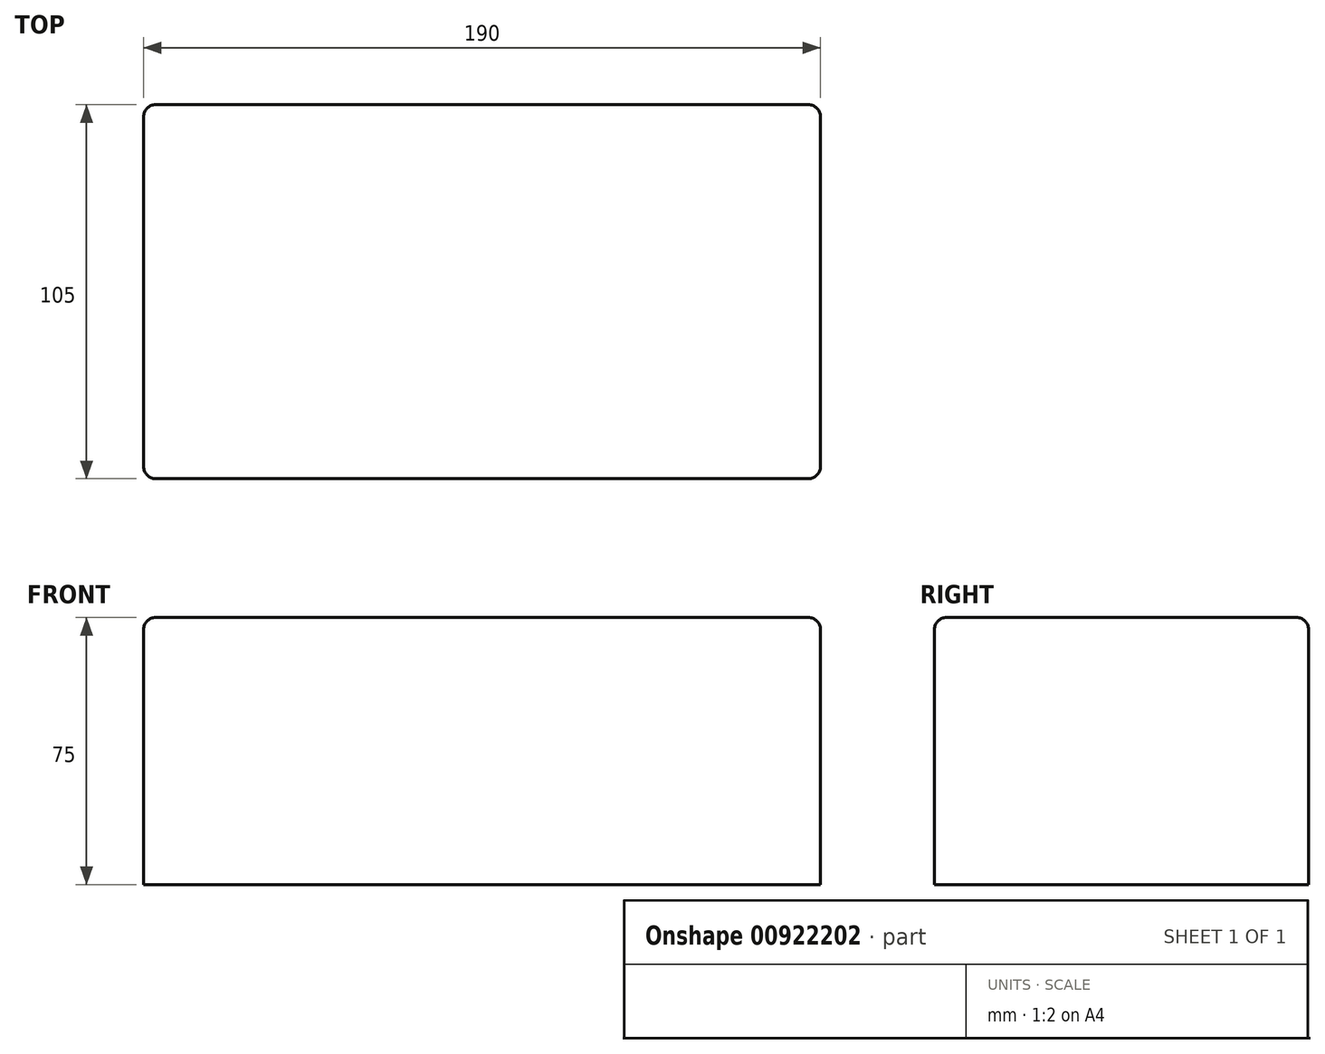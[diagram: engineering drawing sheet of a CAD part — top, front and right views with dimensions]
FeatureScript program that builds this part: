
annotation { "Feature Type Name" : "Feature", "Feature Type Description" : "" }
export const myFeature = defineFeature(function(context is Context, id is Id, definition is map)
    precondition{}
    {
        {
            var Q0;
            Q0=qCreatedBy(makeId("Top.planeOp"),FACE);
            var sketch = newSketch(context, id + "F0", { "sketchPlane" : qUnion([Q0])});
            skLineSegment(sketch, "E0.bottom", {"start": v(-95, 52.5) * mm, "end": v(95, 52.5) * mm});
            skLineSegment(sketch, "E0.top", {"start": v(-95, -52.5) * mm, "end": v(95, -52.5) * mm});
            skLineSegment(sketch, "E0.left", {"start": v(-95, 52.5) * mm, "end": v(-95, -52.5) * mm});
            skLineSegment(sketch, "E0.right", {"start": v(95, 52.5) * mm, "end": v(95, -52.5) * mm});
            skPoint(sketch, "E0.middle", {"position": v(0, 0) * mm});
            skSolve(sketch);
        }
        {
            var Q0;
            Q0 = qSketchRegion(id + "F0", true);
            extrude(context, id + "F1", {"entities" : qUnion([Q0]), "depth" : 75 * mm, "offsetDistance" : 25 * mm});
        }
        {
            var Q0;
            Q0=makeQuery(id+"F1.opExtrude","CAP_EDGE",EDGE,{"disambiguationData":[OSD([sQuery(id+"F0.wireOp",EDGE,"E0.top")])],"isStart":false});
            var Q1;
            Q1=makeQuery(id+"F1.opExtrude","CAP_EDGE",EDGE,{"disambiguationData":[OSD([sQuery(id+"F0.wireOp",EDGE,"E0.left")])],"isStart":false});
            var Q2;
            Q2=makeQuery(id+"F1.opExtrude","CAP_EDGE",EDGE,{"disambiguationData":[OSD([sQuery(id+"F0.wireOp",EDGE,"E0.bottom")])],"isStart":false});
            var Q3;
            Q3=makeQuery(id+"F1.opExtrude","CAP_EDGE",EDGE,{"disambiguationData":[OSD([sQuery(id+"F0.wireOp",EDGE,"E0.right")])],"isStart":false});
            var Q4;
            Q4=makeQuery(id+"F1.opExtrude","SWEPT_EDGE",EDGE,{"disambiguationData":[OSD([sQuery(id+"F0.wireOp",EDGE,"E0.top"),sQuery(id+"F0.wireOp",EDGE,"E0.right")])]});
            var Q5;
            Q5=makeQuery(id+"F1.opExtrude","SWEPT_EDGE",EDGE,{"disambiguationData":[OSD([sQuery(id+"F0.wireOp",EDGE,"E0.top"),sQuery(id+"F0.wireOp",EDGE,"E0.left")])]});
            var Q6;
            Q6=makeQuery(id+"F1.opExtrude","SWEPT_EDGE",EDGE,{"disambiguationData":[OSD([sQuery(id+"F0.wireOp",EDGE,"E0.bottom"),sQuery(id+"F0.wireOp",EDGE,"E0.left")])]});
            var Q7;
            Q7=makeQuery(id+"F1.opExtrude","SWEPT_EDGE",EDGE,{"disambiguationData":[OSD([sQuery(id+"F0.wireOp",EDGE,"E0.bottom"),sQuery(id+"F0.wireOp",EDGE,"E0.right")])]});
            fillet(context, id + "F2", {"entities" : qUnion([Q0, Q1, Q2, Q3, Q4, Q5, Q6, Q7]), "radius" : 3.38 * mm, "tangentPropagation" : true, "allowEdgeOverflow" : false});
        }
    });
